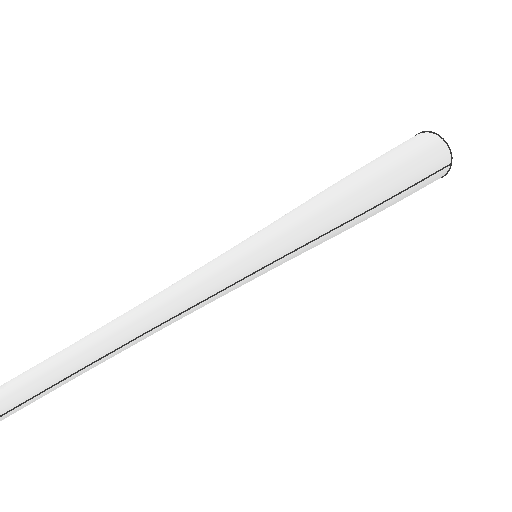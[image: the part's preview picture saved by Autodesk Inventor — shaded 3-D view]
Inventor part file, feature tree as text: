
AUTODESK INVENTOR PART (.ipt)
format: ipt  version: 2025 (Build 290162000, 162)  size: 215,040 bytes
history: native  units: mm
features: sketch x10, plane x5, loft x2
ambient origin geometry x8: Origin, YZ Plane, XZ Plane, XY Plane, X Axis, Y Axis, Z Axis, Center Point
bodies: Body1 (feature_tree)
feature tree (17):
  sketch  "Sketch3"  dims[d9=50.0mm d11=500.0mm]
  plane  "Work Plane2"
  sketch  "Sketch4"  dims[d12=20.0mm d18=47.0mm]
  plane  "Work Plane3"
  sketch  "Sketch5"  dims[d19=17.0mm]
  sketch  "Sketch6"  dims[d24=125.0mm]
  plane  "Work Plane4"
  plane  "Work Plane5"
  plane  "Work Plane6"
  sketch  "Sketch7"  dims[d25=250.0mm]
  sketch  "Sketch8"  dims[d26=375.0mm]
  sketch  "Sketch9"  dims[d27=43.483mm]
  sketch  "Sketch10"  dims[d29=32.43mm]
  sketch  "Sketch11"  dims[d31=23.7694mm]
  sketch  "Sketch12"  dims[d33=40.483mm d34=29.43mm d35=20.7694mm d36=0.0mm d37=90.0deg d38=0.0mm d39=90.0deg d40=0.0mm d41=90.0deg d42=0.0mm d43=90.0deg d44=0.0mm d45=90.0deg d46=0.0mm d47=90.0deg d48=0.0mm d49=90.0deg d50=0.0mm d51=90.0deg d52=0.0mm d53=90.0deg d54=0.0mm d55=90.0deg]
  loft  "Loft3"
  loft  "Loft4"
